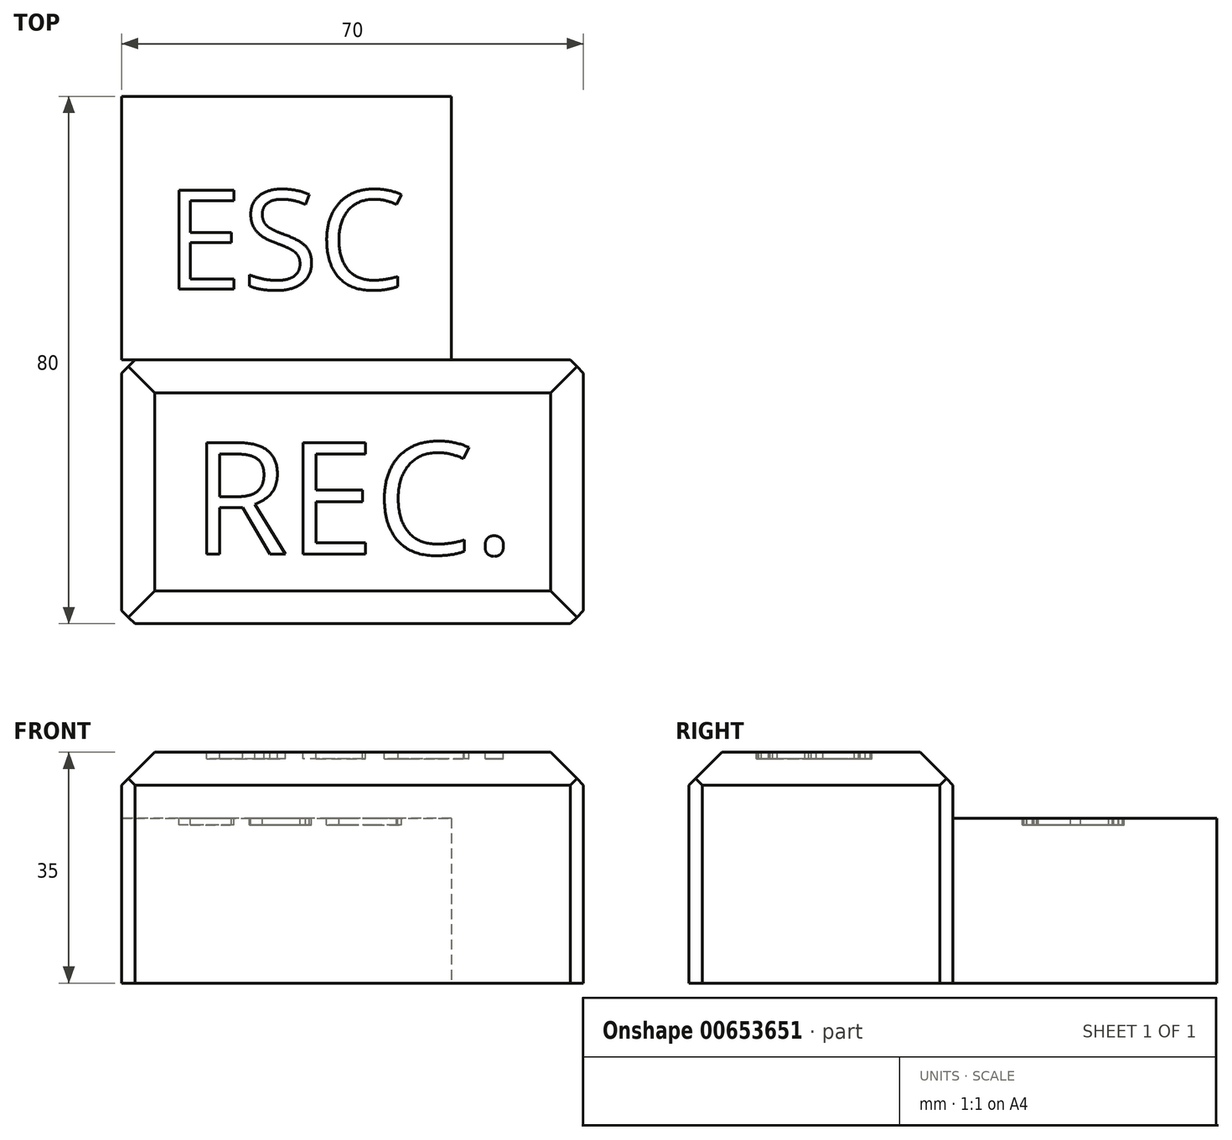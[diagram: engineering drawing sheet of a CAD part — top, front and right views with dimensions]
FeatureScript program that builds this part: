
annotation { "Feature Type Name" : "Feature", "Feature Type Description" : "" }
export const myFeature = defineFeature(function(context is Context, id is Id, definition is map)
    precondition{}
    {
        {
            var Q0;
            Q0=qCreatedBy(makeId("Top.planeOp"),FACE);
            var sketch = newSketch(context, id + "F0", { "sketchPlane" : qUnion([Q0])});
            skLineSegment(sketch, "E0.bottom", {"start": v(0, 0) * mm, "end": v(70, 0) * mm});
            skLineSegment(sketch, "E0.top", {"start": v(0, 40) * mm, "end": v(70, 40) * mm});
            skLineSegment(sketch, "E0.left", {"start": v(0, 0) * mm, "end": v(0, 40) * mm});
            skLineSegment(sketch, "E0.right", {"start": v(70, 0) * mm, "end": v(70, 40) * mm});
            skSolve(sketch);
        }
        {
            var Q0;
            Q0 = qSketchRegion(id + "F0", true);
            extrude(context, id + "F1", {"entities" : qUnion([Q0]), "depth" : 35 * mm, "offsetDistance" : 25 * mm});
        }
        {
            var Q0;
            Q0=makeQuery(id+"F1.opExtrude","CAP_FACE",FACE,{"disambiguationData":[OSD([sQuery(id+"F0.wireOp",EDGE,"E0.bottom"),sQuery(id+"F0.wireOp",EDGE,"E0.top"),sQuery(id+"F0.wireOp",EDGE,"E0.left"),sQuery(id+"F0.wireOp",EDGE,"E0.right")])],"isStart":false});
            chamfer(context, id + "F2", {"entities" : qUnion([Q0]), "width" : 5 * mm, "tangentPropagation" : true});
        }
        {
            var Q0;
            Q0=makeQuery(id+"F1.opExtrude","SWEPT_EDGE",EDGE,{"disambiguationData":[OSD([sQuery(id+"F0.wireOp",EDGE,"E0.top"),sQuery(id+"F0.wireOp",EDGE,"E0.left")])]});
            var Q1;
            Q1=makeQuery(id+"F1.opExtrude","SWEPT_EDGE",EDGE,{"disambiguationData":[OSD([sQuery(id+"F0.wireOp",EDGE,"E0.bottom"),sQuery(id+"F0.wireOp",EDGE,"E0.left")])]});
            var Q2;
            Q2=makeQuery(id+"F1.opExtrude","SWEPT_EDGE",EDGE,{"disambiguationData":[OSD([sQuery(id+"F0.wireOp",EDGE,"E0.bottom"),sQuery(id+"F0.wireOp",EDGE,"E0.right")])]});
            var Q3;
            Q3=makeQuery(id+"F1.opExtrude","SWEPT_EDGE",EDGE,{"disambiguationData":[OSD([sQuery(id+"F0.wireOp",EDGE,"E0.top"),sQuery(id+"F0.wireOp",EDGE,"E0.right")])]});
            chamfer(context, id + "F3", {"entities" : qUnion([Q0, Q1, Q2, Q3]), "width" : 2 * mm, "tangentPropagation" : true});
        }
        {
            var Q0;
            Q0=makeQuery(id+"F1.opExtrude","CAP_FACE",FACE,{"disambiguationData":[OSD([sQuery(id+"F0.wireOp",EDGE,"E0.bottom"),sQuery(id+"F0.wireOp",EDGE,"E0.top"),sQuery(id+"F0.wireOp",EDGE,"E0.left"),sQuery(id+"F0.wireOp",EDGE,"E0.right")])],"isStart":true});
            var sketch = newSketch(context, id + "F4", { "sketchPlane" : qUnion([Q0])});
            skLineSegment(sketch, "E1.bottom", {"start": v(50, -40) * mm, "end": v(0, -40) * mm});
            skLineSegment(sketch, "E1.top", {"start": v(50, -80) * mm, "end": v(0, -80) * mm});
            skLineSegment(sketch, "E1.left", {"start": v(50, -40) * mm, "end": v(50, -80) * mm});
            skLineSegment(sketch, "E1.right", {"start": v(0, -40) * mm, "end": v(0, -80) * mm});
            skSolve(sketch);
        }
        {
            var Q0;
            Q0 = qSketchRegion(id + "F4", true);
            extrude(context, id + "F5", {"entities" : qUnion([Q0]), "operationType" : NewBodyOperationType.ADD, "oppositeDirection" : true, "depth" : 25 * mm, "offsetDistance" : 25 * mm});
        }
        {
            var Q0;
            Q0=makeQuery(id+"F5.opExtrude","CAP_FACE",FACE,{"disambiguationData":[OSD([sQuery(id+"F4.wireOp",EDGE,"E1.bottom"),sQuery(id+"F4.wireOp",EDGE,"E1.top"),sQuery(id+"F4.wireOp",EDGE,"E1.left"),sQuery(id+"F4.wireOp",EDGE,"E1.right")])],"isStart":false});
            var sketch = newSketch(context, id + "F6", { "sketchPlane" : qUnion([Q0])});
            skText(sketch, "E2", { "text": "ESC", "fontName": "OpenSans-Regular.ttf"});
            const initialGuessF6  = {"E2": [0.00662, 0.05075, 1, 0, 0.0151]};
            skSetInitialGuess(sketch, initialGuessF6);
            skSolve(sketch);
        }
        {
            var Q0;
            Q0 = qSketchRegion(id + "F6", true);
            extrude(context, id + "F7", {"entities" : qUnion([Q0]), "operationType" : NewBodyOperationType.REMOVE, "oppositeDirection" : true, "depth" : 1 * mm, "offsetDistance" : 25 * mm});
        }
        {
            var Q0;
            Q0=makeQuery(id+"F1.opExtrude","CAP_FACE",FACE,{"disambiguationData":[OSD([sQuery(id+"F0.wireOp",EDGE,"E0.bottom"),sQuery(id+"F0.wireOp",EDGE,"E0.top"),sQuery(id+"F0.wireOp",EDGE,"E0.left"),sQuery(id+"F0.wireOp",EDGE,"E0.right")])],"isStart":false});
            var sketch = newSketch(context, id + "F8", { "sketchPlane" : qUnion([Q0])});
            skText(sketch, "E3", { "text": "REC.", "fontName": "OpenSans-Regular.ttf"});
            const initialGuessF8  = {"E3": [0.01055, 0.01055, 1, 0, 0.01706]};
            skSetInitialGuess(sketch, initialGuessF8);
            skSolve(sketch);
        }
        {
            var Q0;
            Q0 = qSketchRegion(id + "F8", true);
            extrude(context, id + "F9", {"entities" : qUnion([Q0]), "operationType" : NewBodyOperationType.REMOVE, "oppositeDirection" : true, "depth" : 1 * mm, "offsetDistance" : 25 * mm});
        }
    });
